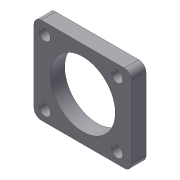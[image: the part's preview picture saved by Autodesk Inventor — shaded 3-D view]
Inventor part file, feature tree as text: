
AUTODESK INVENTOR PART (.ipt)
format: ipt  version: 2012 (Build 160160000, 160)  size: 109,056 bytes
history: native  units: in
note: dims shown in document units (in); Inventor stores cm internally (conversion verified against a paired STEP export)
features: extrude x1, fillet x1, sketch x1
ambient origin geometry x8: Origin, YZ Plane, XZ Plane, XY Plane, X Axis, Y Axis, Z Axis, Center Point
bodies: Solid1 (feature_tree)
feature tree (3):
  extrude  "Extrusion1"  Depth=1.6875in
  fillet  "Fillet1"  Radius=1.5in
  sketch  "Sketch1"  dims[d0=1.125in d1=1.6875in d2=1.5in d3=0.8438in d4=0.75in d5=0.192in d6=0.1875in d7=0.1875in d8=0.25in d9=0.1875in d10=1.25in d11=0.25in d12=0.0in d13=0.125in]
